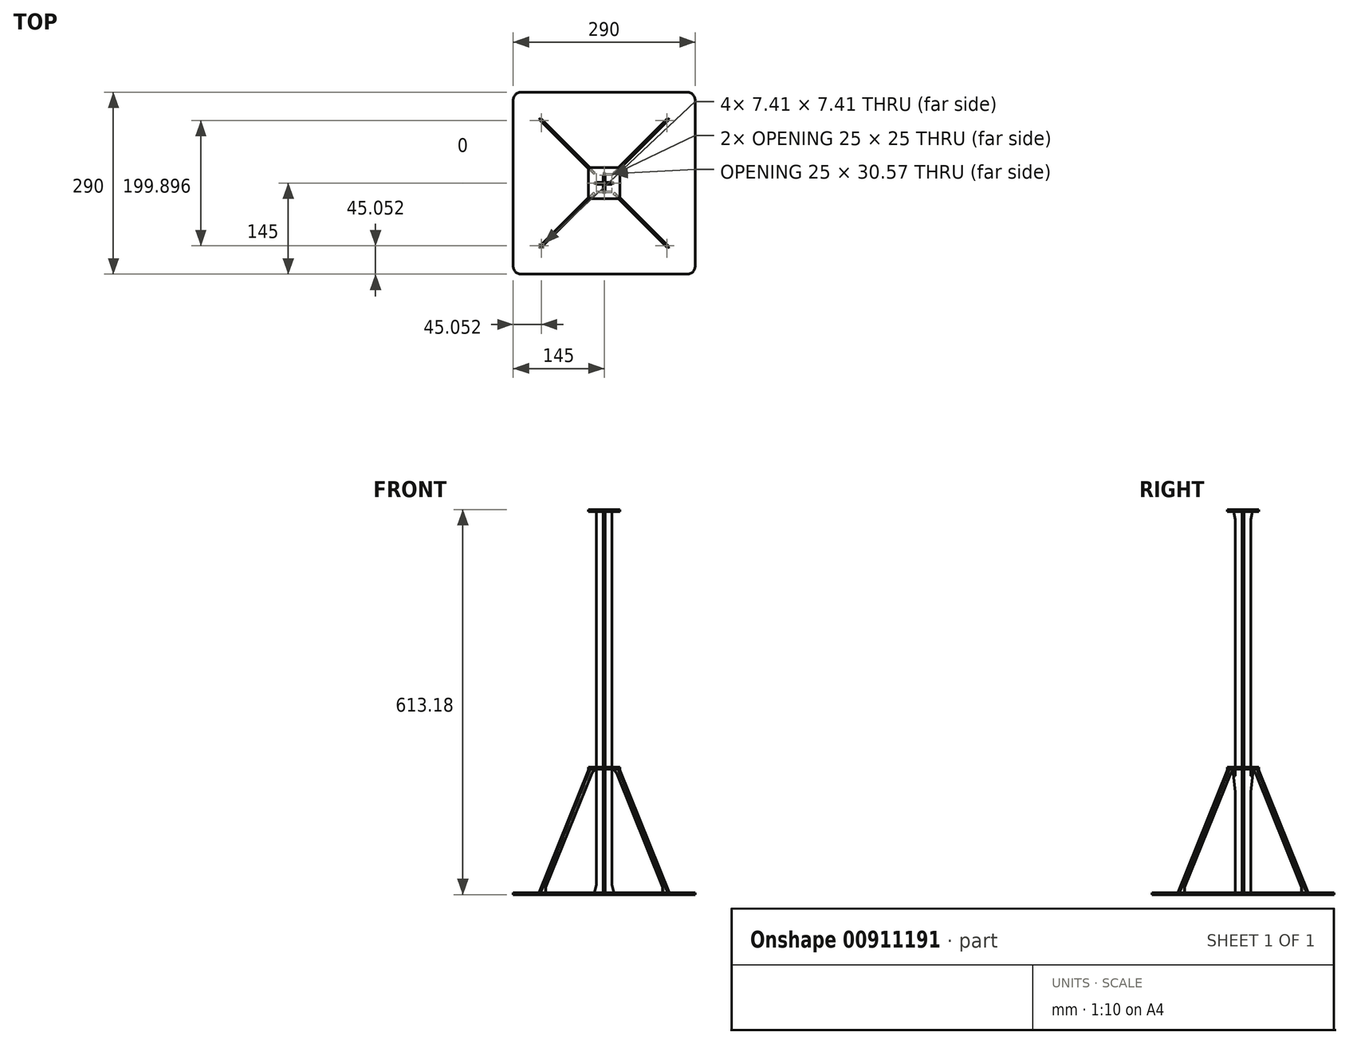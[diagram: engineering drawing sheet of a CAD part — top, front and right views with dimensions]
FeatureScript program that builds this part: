
annotation { "Feature Type Name" : "Feature", "Feature Type Description" : "" }
export const myFeature = defineFeature(function(context is Context, id is Id, definition is map)
    precondition{}
    {
        {
            assignVariable(context, id + "F0", {"variableType" : VariableType.LENGTH, "name" : "Thickness", "lengthValue" : 3.17 * mm});
        }
        {
            var Q0;
            Q0=qCreatedBy(makeId("Top.planeOp"),FACE);
            var sketch = newSketch(context, id + "F1", { "sketchPlane" : qUnion([Q0])});
            skLineSegment(sketch, "E0.bottom", {"start": v(-145, 145) * mm, "end": v(145, 145) * mm});
            skLineSegment(sketch, "E0.top", {"start": v(-145, -145) * mm, "end": v(145, -145) * mm});
            skLineSegment(sketch, "E0.left", {"start": v(-145, 145) * mm, "end": v(-145, -145) * mm});
            skLineSegment(sketch, "E0.right", {"start": v(145, 145) * mm, "end": v(145, -145) * mm});
            skPoint(sketch, "E0.middle", {"position": v(0, 0) * mm});
            skCircle(sketch, "E1", {"center": v(0, 0) * mm, "radius": 145 * mm});
            skLineSegment(sketch, "E2", {"start": v(0, 0) * mm, "end": v(145, 145) * mm, "construction": true});
            skLineSegment(sketch, "E3", {"start": v(0, 0) * mm, "end": v(-145, 145) * mm, "construction": true});
            skLineSegment(sketch, "E4", {"start": v(0, 0) * mm, "end": v(145, -145) * mm, "construction": true});
            skLineSegment(sketch, "E5", {"start": v(0, 0) * mm, "end": v(-145, -145) * mm, "construction": true});
            skSolve(sketch);
        }
        {
            var Q0;
            Q0 = qSketchRegion(id + "F1", true);
            extrude(context, id + "F2", {"entities" : qUnion([Q0]), "depth" : getVariable(context, 'Thickness'), "offsetDistance" : 25.4 * mm});
        }
        {
            var Q0;
            Q0=qCreatedBy(makeId("Right.planeOp"),FACE);
            var sketch = newSketch(context, id + "F3", { "sketchPlane" : qUnion([Q0])});
            skLineSegment(sketch, "E6.bottom", {"start": v(-12.5, 0) * mm, "end": v(12.5, 0) * mm});
            skLineSegment(sketch, "E6.top", {"start": v(-12.5, 613.18) * mm, "end": v(12.5, 613.18) * mm});
            skLineSegment(sketch, "E6.left", {"start": v(-12.5, 0) * mm, "end": v(-12.5, 163.77) * mm});
            skLineSegment(sketch, "E6.right", {"start": v(12.5, 189.19) * mm, "end": v(12.5, 597.3) * mm});
            skPoint(sketch, "E6.middle", {"position": v(0, 306.59) * mm});
            skLineSegment(sketch, "E7", {"start": v(12.5, 203.18) * mm, "end": v(-12.5, 203.18) * mm, "construction": true});
            skLineSegment(sketch, "E8.bottom", {"start": v(25, 203.18) * mm, "end": v(-25, 203.18) * mm, "construction": true});
            skLineSegment(sketch, "E8.top", {"start": v(25, 200) * mm, "end": v(-25, 200) * mm, "construction": true});
            skLineSegment(sketch, "E8.left", {"start": v(25, 203.18) * mm, "end": v(25, 200) * mm, "construction": true});
            skLineSegment(sketch, "E8.right", {"start": v(-25, 203.18) * mm, "end": v(-25, 200) * mm, "construction": true});
            skPoint(sketch, "E8.middle", {"position": v(0, 201.59) * mm});
            skPoint(sketch, "E8.middle.positionSnap0", {"position": v(0, 203.18) * mm});
            skPoint(sketch, "E8.cornerSnap0", {"position": v(0, 203.18) * mm});
            skPoint(sketch, "E8.centerSnap0", {"position": v(0, 203.18) * mm});
            skLineSegment(sketch, "E9.bottom", {"start": v(-15, 613.18) * mm, "end": v(15, 613.18) * mm, "construction": true});
            skLineSegment(sketch, "E9.top", {"start": v(-15, 610) * mm, "end": v(15, 610) * mm, "construction": true});
            skLineSegment(sketch, "E9.left", {"start": v(-15, 613.18) * mm, "end": v(-15, 610) * mm, "construction": true});
            skLineSegment(sketch, "E9.right", {"start": v(15, 613.18) * mm, "end": v(15, 610) * mm, "construction": true});
            skPoint(sketch, "E9.middle", {"position": v(0, 611.59) * mm});
            skLineSegment(sketch, "E10", {"start": v(15, 610) * mm, "end": v(12.5, 597.3) * mm});
            skLineSegment(sketch, "E11", {"start": v(16.48, 200) * mm, "end": v(12.5, 163.8) * mm});
            skLineSegment(sketch, "E12", {"start": v(14.09, 200) * mm, "end": v(12.9, 189.16) * mm});
            skArc(sketch, "E13.filletArc", {"start": v(12.5, 189.19) * mm, "mid": v(12.69, 188.99) * mm, "end": v(12.9, 189.16) * mm});
            skLineSegment(sketch, "E14", {"start": v(12.5, 163.77) * mm, "end": v(12.5, 0) * mm});
            skPoint(sketch, "E15.visualSharp", {"position": v(12.5, 163.79) * mm});
            skArc(sketch, "E15.filletArc", {"start": v(12.5, 163.8) * mm, "mid": v(12.5, 163.79) * mm, "end": v(12.5, 163.77) * mm});
            skLineSegment(sketch, "E16", {"start": v(16.48, 200) * mm, "end": v(14.09, 200) * mm});
            skLineSegment(sketch, "E17.trimOffspring", {"start": v(12.5, 610) * mm, "end": v(12.5, 613.18) * mm});
            skLineSegment(sketch, "E18", {"start": v(15, 610) * mm, "end": v(12.5, 610) * mm});
            skLineSegment(sketch, "E19.MirrorCS", {"start": v(-14.09, 200) * mm, "end": v(-12.9, 189.16) * mm});
            skLineSegment(sketch, "E20.MirrorCS", {"start": v(-16.48, 200) * mm, "end": v(-12.5, 163.8) * mm});
            skArc(sketch, "E21.MirrorCS", {"start": v(-12.5, 189.19) * mm, "mid": v(-12.69, 188.99) * mm, "end": v(-12.9, 189.16) * mm});
            skArc(sketch, "E22.MirrorCS", {"start": v(-12.5, 163.8) * mm, "mid": v(-12.5, 163.79) * mm, "end": v(-12.5, 163.77) * mm});
            skLineSegment(sketch, "E23.MirrorCS", {"start": v(-15, 610) * mm, "end": v(-12.5, 597.3) * mm});
            skLineSegment(sketch, "E24", {"start": v(-12.5, 610) * mm, "end": v(-15, 610) * mm});
            skLineSegment(sketch, "E25", {"start": v(-14.09, 200) * mm, "end": v(-16.48, 200) * mm});
            skLineSegment(sketch, "E26.trimOffspring", {"start": v(-12.5, 189.19) * mm, "end": v(-12.5, 597.3) * mm});
            skLineSegment(sketch, "E27.bottom", {"start": v(-1.59, 613.18) * mm, "end": v(1.59, 613.18) * mm});
            skLineSegment(sketch, "E27.top", {"start": v(-1.59, 308.18) * mm, "end": v(1.59, 308.18) * mm});
            skLineSegment(sketch, "E27.left", {"start": v(-1.59, 613.18) * mm, "end": v(-1.59, 308.18) * mm});
            skLineSegment(sketch, "E27.right", {"start": v(1.59, 613.18) * mm, "end": v(1.59, 308.18) * mm});
            skPoint(sketch, "E27.middle", {"position": v(0, 460.68) * mm});
            skLineSegment(sketch, "E28.trimOffspring", {"start": v(-12.5, 610) * mm, "end": v(-12.5, 613.18) * mm});
            skLineSegment(sketch, "E29", {"start": v(0, 306.59) * mm, "end": v(0, 0) * mm, "construction": true});
            skSolve(sketch);
        }
        {
            var Q0;
            Q0=makeQuery(id+"F3.imprint","IMPRINT",FACE,{"disambiguationData":[TD([[makeQuery(id+"F3.imprint","IMPRINT",EDGE,{"derivedFrom":sQuery(id+"F3.wireOp",EDGE,"E6.bottom")}),1.0]])]});
            extrude(context, id + "F4", {"entities" : qUnion([Q0]), "endBound" : BoundingType.SYMMETRIC, "depth" : getVariable(context, 'Thickness'), "offsetDistance" : 25.4 * mm});
        }
        {
            var Q0;
            Q0=qCreatedBy(makeId("Front.planeOp"),FACE);
            var sketch = newSketch(context, id + "F5", { "sketchPlane" : qUnion([Q0])});
            skLineSegment(sketch, "E30.bottom", {"start": v(-12.5, 0) * mm, "end": v(12.5, 0) * mm});
            skLineSegment(sketch, "E30.top", {"start": v(-12.5, 613.18) * mm, "end": v(12.5, 613.18) * mm});
            skLineSegment(sketch, "E30.left", {"start": v(-12.5, 0) * mm, "end": v(-12.5, 3.18) * mm});
            skLineSegment(sketch, "E30.right", {"start": v(12.5, 0) * mm, "end": v(12.5, 3.18) * mm});
            skPoint(sketch, "E30.middle", {"position": v(0, 306.59) * mm});
            skLineSegment(sketch, "E31", {"start": v(12.5, 15.87) * mm, "end": v(15.68, 3.18) * mm});
            skLineSegment(sketch, "E32", {"start": v(15.68, 3.18) * mm, "end": v(12.5, 3.18) * mm});
            skLineSegment(sketch, "E33.trimOffspring", {"start": v(12.5, 15.88) * mm, "end": v(12.5, 613.18) * mm});
            skLineSegment(sketch, "E34.MirrorCS", {"start": v(-12.5, 15.87) * mm, "end": v(-15.68, 3.18) * mm});
            skLineSegment(sketch, "E35", {"start": v(-15.68, 3.18) * mm, "end": v(-12.5, 3.18) * mm});
            skLineSegment(sketch, "E36.trimOffspring", {"start": v(-12.5, 15.88) * mm, "end": v(-12.5, 613.18) * mm});
            skSolve(sketch);
        }
        {
            var Q0;
            Q0 = qSketchRegion(id + "F5", true);
            extrude(context, id + "F6", {"entities" : qUnion([Q0]), "endBound" : BoundingType.SYMMETRIC, "depth" : getVariable(context, 'Thickness'), "offsetDistance" : 25.4 * mm});
        }
        {
            var Q0;
            Q0=makeQuery(id+"F4.opExtrude","SWEPT_BODY",BODY,{"disambiguationData":[OSD([sQuery(id+"F3.wireOp",EDGE,"E6.bottom"),sQuery(id+"F3.wireOp",EDGE,"E6.top"),sQuery(id+"F3.wireOp",EDGE,"E6.left"),sQuery(id+"F3.wireOp",EDGE,"E6.right"),sQuery(id+"F3.wireOp",EDGE,"E10"),sQuery(id+"F3.wireOp",EDGE,"E11"),sQuery(id+"F3.wireOp",EDGE,"E12"),sQuery(id+"F3.wireOp",EDGE,"E13.filletArc"),sQuery(id+"F3.wireOp",EDGE,"E14"),sQuery(id+"F3.wireOp",EDGE,"E15.filletArc"),sQuery(id+"F3.wireOp",EDGE,"E16"),sQuery(id+"F3.wireOp",EDGE,"E17.trimOffspring"),sQuery(id+"F3.wireOp",EDGE,"E18"),sQuery(id+"F3.wireOp",EDGE,"E19.MirrorCS"),sQuery(id+"F3.wireOp",EDGE,"E20.MirrorCS"),sQuery(id+"F3.wireOp",EDGE,"E21.MirrorCS"),sQuery(id+"F3.wireOp",EDGE,"E22.MirrorCS"),sQuery(id+"F3.wireOp",EDGE,"E23.MirrorCS"),sQuery(id+"F3.wireOp",EDGE,"E24"),sQuery(id+"F3.wireOp",EDGE,"E25"),sQuery(id+"F3.wireOp",EDGE,"E26.trimOffspring"),sQuery(id+"F3.wireOp",EDGE,"E27.top"),sQuery(id+"F3.wireOp",EDGE,"E27.left"),sQuery(id+"F3.wireOp",EDGE,"E27.right"),sQuery(id+"F3.wireOp",EDGE,"E28.trimOffspring")])]});
            var Q1;
            Q1=makeQuery(id+"F6.opExtrude","SWEPT_BODY",BODY,{"disambiguationData":[OSD([sQuery(id+"F5.wireOp",EDGE,"E30.bottom"),sQuery(id+"F5.wireOp",EDGE,"E30.top"),sQuery(id+"F5.wireOp",EDGE,"E30.left"),sQuery(id+"F5.wireOp",EDGE,"E30.right"),sQuery(id+"F5.wireOp",EDGE,"E31"),sQuery(id+"F5.wireOp",EDGE,"E32"),sQuery(id+"F5.wireOp",EDGE,"E33.trimOffspring"),sQuery(id+"F5.wireOp",EDGE,"E34.MirrorCS"),sQuery(id+"F5.wireOp",EDGE,"E35"),sQuery(id+"F5.wireOp",EDGE,"E36.trimOffspring")])]});
            booleanBodies(context, id + "F7", {"operationType" : BooleanOperationType.SUBTRACTION, "tools" : qUnion([Q0]), "targets" : qUnion([Q1]), "keepTools" : true});
        }
        {
            var Q0;
            Q0=makeQuery(id+"F4.opExtrude","SWEPT_FACE",FACE,{"disambiguationData":[OSD([sQuery(id+"F3.wireOp",EDGE,"E24")])]});
            var sketch = newSketch(context, id + "F8", { "sketchPlane" : qUnion([Q0])});
            skLineSegment(sketch, "E37.bottom", {"start": v(-25, 25) * mm, "end": v(25, 25) * mm});
            skLineSegment(sketch, "E37.top", {"start": v(-25, -25) * mm, "end": v(25, -25) * mm});
            skLineSegment(sketch, "E37.left", {"start": v(-25, 25) * mm, "end": v(-25, -25) * mm});
            skLineSegment(sketch, "E37.right", {"start": v(25, 25) * mm, "end": v(25, -25) * mm});
            skPoint(sketch, "E37.middle", {"position": v(0, 0) * mm});
            skSolve(sketch);
        }
        {
            var Q0;
            Q0 = qSketchRegion(id + "F8", true);
            extrude(context, id + "F9", {"entities" : qUnion([Q0]), "depth" : getVariable(context, 'Thickness'), "offsetDistance" : 25.4 * mm});
        }
        {
            var Q0;
            Q0=makeQuery(id+"F4.opExtrude","SWEPT_FACE",FACE,{"disambiguationData":[OSD([sQuery(id+"F3.wireOp",EDGE,"E16")])]});
            var sketch = newSketch(context, id + "F10", { "sketchPlane" : qUnion([Q0])});
            skLineSegment(sketch, "E38.bottom", {"start": v(25, 25) * mm, "end": v(-25, 25) * mm});
            skLineSegment(sketch, "E38.top", {"start": v(25, -25) * mm, "end": v(-25, -25) * mm});
            skLineSegment(sketch, "E38.left", {"start": v(25, 25) * mm, "end": v(25, -25) * mm});
            skLineSegment(sketch, "E38.right", {"start": v(-25, 25) * mm, "end": v(-25, -25) * mm});
            skPoint(sketch, "E38.middle", {"position": v(0, 0) * mm});
            skPoint(sketch, "E39.0", {"position": v(-1.59, 15.29) * mm});
            skPoint(sketch, "E40.0", {"position": v(0, 16.48) * mm});
            skPoint(sketch, "E41", {"position": v(0, 15.29) * mm});
            skLineSegment(sketch, "E42.bottom", {"start": v(-1.59, 15.29) * mm, "end": v(1.59, 15.29) * mm});
            skLineSegment(sketch, "E42.top", {"start": v(-1.59, -15.29) * mm, "end": v(1.59, -15.29) * mm});
            skLineSegment(sketch, "E42.left", {"start": v(-1.59, 15.29) * mm, "end": v(-1.59, -15.29) * mm});
            skLineSegment(sketch, "E42.right", {"start": v(1.59, 15.29) * mm, "end": v(1.59, -15.29) * mm});
            skSolve(sketch);
        }
        {
            var Q0;
            Q0 = qSketchRegion(id + "F10", true);
            extrude(context, id + "F11", {"entities" : qUnion([Q0]), "depth" : getVariable(context, 'Thickness'), "offsetDistance" : 25.4 * mm});
        }
        {
            var Q0;
            Q0=makeQuery(id+"F9.opExtrude","SWEPT_EDGE",EDGE,{"disambiguationData":[OSD([sQuery(id+"F8.wireOp",EDGE,"E37.top"),sQuery(id+"F8.wireOp",EDGE,"E37.left")])]});
            var Q1;
            Q1=makeQuery(id+"F9.opExtrude","SWEPT_EDGE",EDGE,{"disambiguationData":[OSD([sQuery(id+"F8.wireOp",EDGE,"E37.top"),sQuery(id+"F8.wireOp",EDGE,"E37.right")])]});
            var Q2;
            Q2=makeQuery(id+"F9.opExtrude","SWEPT_EDGE",EDGE,{"disambiguationData":[OSD([sQuery(id+"F8.wireOp",EDGE,"E37.bottom"),sQuery(id+"F8.wireOp",EDGE,"E37.right")])]});
            var Q3;
            Q3=makeQuery(id+"F9.opExtrude","SWEPT_EDGE",EDGE,{"disambiguationData":[OSD([sQuery(id+"F8.wireOp",EDGE,"E37.bottom"),sQuery(id+"F8.wireOp",EDGE,"E37.left")])]});
            var Q4;
            Q4=makeQuery(id+"F11.opExtrude","SWEPT_EDGE",EDGE,{"disambiguationData":[OSD([sQuery(id+"F10.wireOp",EDGE,"E38.bottom"),sQuery(id+"F10.wireOp",EDGE,"E38.right")])]});
            var Q5;
            Q5=makeQuery(id+"F11.opExtrude","SWEPT_EDGE",EDGE,{"disambiguationData":[OSD([sQuery(id+"F10.wireOp",EDGE,"E38.bottom"),sQuery(id+"F10.wireOp",EDGE,"E38.left")])]});
            var Q6;
            Q6=makeQuery(id+"F11.opExtrude","SWEPT_EDGE",EDGE,{"disambiguationData":[OSD([sQuery(id+"F10.wireOp",EDGE,"E38.top"),sQuery(id+"F10.wireOp",EDGE,"E38.right")])]});
            var Q7;
            Q7=makeQuery(id+"F11.opExtrude","SWEPT_EDGE",EDGE,{"disambiguationData":[OSD([sQuery(id+"F10.wireOp",EDGE,"E38.top"),sQuery(id+"F10.wireOp",EDGE,"E38.left")])]});
            chamfer(context, id + "F12", {"entities" : qUnion([Q0, Q1, Q2, Q3, Q4, Q5, Q6, Q7]), "width" : 3.17 * mm, "tangentPropagation" : true});
        }
        {
            var Q0;
            Q0=sQuery(id+"F1.wireOp",EDGE,"E5");
            cPlane(context, id + "F13", {"entities" : qUnion([Q0]), "cplaneType" : CPlaneType.LINE_ANGLE, "offset" : 25.4 * mm, "angle" : 90 * degree, "width" : 152.4 * mm, "height" : 152.4 * mm});
        }
        {
            var Q0;
            Q0=qCreatedBy(id+"F13.planeOp",FACE);
            var sketch = newSketch(context, id + "F14", { "sketchPlane" : qUnion([Q0])});
            skPoint(sketch, "E43.0", {"position": v(-31.3, 203.18) * mm});
            skLineSegment(sketch, "E44", {"start": v(-33.11, 200) * mm, "end": v(-145, 3.17) * mm});
            skLineSegment(sketch, "E45", {"start": v(-132.93, 11.55) * mm, "end": v(-29.42, 193.65) * mm});
            skLineSegment(sketch, "E46", {"start": v(-132.93, 11.55) * mm, "end": v(-132.93, 3.18) * mm});
            skLineSegment(sketch, "E47", {"start": v(-145, 3.18) * mm, "end": v(-145, 0) * mm});
            skLineSegment(sketch, "E48", {"start": v(-145, 0) * mm, "end": v(-137.7, 0) * mm});
            skLineSegment(sketch, "E49", {"start": v(-137.7, 0) * mm, "end": v(-137.7, 3.18) * mm});
            skLineSegment(sketch, "E50", {"start": v(-29.42, 193.65) * mm, "end": v(-22.15, 200) * mm});
            skLineSegment(sketch, "E51.0", {"start": v(-2.25, 200) * mm, "end": v(-33.11, 200) * mm});
            skPoint(sketch, "E52.0", {"position": v(-33.11, 200) * mm});
            skPoint(sketch, "E53.orphan", {"position": v(-24, 203.18) * mm});
            skLineSegment(sketch, "E54", {"start": v(-33.11, 200) * mm, "end": v(-33.11, 203.18) * mm});
            skLineSegment(sketch, "E55", {"start": v(-33.11, 203.18) * mm, "end": v(-25.8, 203.18) * mm});
            skLineSegment(sketch, "E56", {"start": v(-25.8, 203.18) * mm, "end": v(-25.8, 200) * mm});
            skLineSegment(sketch, "E57", {"start": v(-137.7, 3.18) * mm, "end": v(-132.93, 3.18) * mm});
            skLineSegment(sketch, "E58.0", {"start": v(-145, 0) * mm, "end": v(145, 0) * mm});
            skLineSegment(sketch, "E58.1", {"start": v(0, 0) * mm, "end": v(-205.06, 0) * mm});
            skSolve(sketch);
        }
        {
            var Q0;
            Q0 = qSketchRegion(id + "F14", true);
            extrude(context, id + "F15", {"entities" : qUnion([Q0]), "endBound" : BoundingType.SYMMETRIC, "depth" : getVariable(context, 'Thickness'), "offsetDistance" : 25.4 * mm});
        }
        {
            var Q0;
            Q0=makeQuery(id+"F15.opExtrude","SWEPT_BODY",BODY,{"disambiguationData":[OSD([sQuery(id+"F14.wireOp",EDGE,"E44"),sQuery(id+"F14.wireOp",EDGE,"E45"),sQuery(id+"F14.wireOp",EDGE,"E46"),sQuery(id+"F14.wireOp",EDGE,"E47"),sQuery(id+"F14.wireOp",EDGE,"E48"),sQuery(id+"F14.wireOp",EDGE,"E49"),sQuery(id+"F14.wireOp",EDGE,"E50"),sQuery(id+"F14.wireOp",EDGE,"E51.0"),sQuery(id+"F14.wireOp",EDGE,"E54"),sQuery(id+"F14.wireOp",EDGE,"E55"),sQuery(id+"F14.wireOp",EDGE,"E56"),sQuery(id+"F14.wireOp",EDGE,"E57")])]});
            var Q1;
            Q1=sQuery(id+"F3.wireOp",EDGE,"E29");
            circularPattern(context, id + "F16", {"entities" : qUnion([Q0]), "axis" : qUnion([Q1]), "angle" : 360 * degree, "instanceCount" : 4, "equalSpace" : true});
        }
        {
            var Q0;
            Q0=makeQuery(id+"F6.opExtrude","SWEPT_BODY",BODY,{"disambiguationData":[OSD([sQuery(id+"F5.wireOp",EDGE,"E30.bottom"),sQuery(id+"F5.wireOp",EDGE,"E30.top"),sQuery(id+"F5.wireOp",EDGE,"E30.left"),sQuery(id+"F5.wireOp",EDGE,"E30.right"),sQuery(id+"F5.wireOp",EDGE,"E31"),sQuery(id+"F5.wireOp",EDGE,"E32"),sQuery(id+"F5.wireOp",EDGE,"E33.trimOffspring"),sQuery(id+"F5.wireOp",EDGE,"E34.MirrorCS"),sQuery(id+"F5.wireOp",EDGE,"E35"),sQuery(id+"F5.wireOp",EDGE,"E36.trimOffspring")])]});
            var Q1;
            Q1=makeQuery(id+"F4.opExtrude","SWEPT_BODY",BODY,{"disambiguationData":[OSD([sQuery(id+"F3.wireOp",EDGE,"E6.bottom"),sQuery(id+"F3.wireOp",EDGE,"E6.top"),sQuery(id+"F3.wireOp",EDGE,"E6.left"),sQuery(id+"F3.wireOp",EDGE,"E6.right"),sQuery(id+"F3.wireOp",EDGE,"E10"),sQuery(id+"F3.wireOp",EDGE,"E11"),sQuery(id+"F3.wireOp",EDGE,"E12"),sQuery(id+"F3.wireOp",EDGE,"E13.filletArc"),sQuery(id+"F3.wireOp",EDGE,"E14"),sQuery(id+"F3.wireOp",EDGE,"E15.filletArc"),sQuery(id+"F3.wireOp",EDGE,"E16"),sQuery(id+"F3.wireOp",EDGE,"E17.trimOffspring"),sQuery(id+"F3.wireOp",EDGE,"E18"),sQuery(id+"F3.wireOp",EDGE,"E19.MirrorCS"),sQuery(id+"F3.wireOp",EDGE,"E20.MirrorCS"),sQuery(id+"F3.wireOp",EDGE,"E21.MirrorCS"),sQuery(id+"F3.wireOp",EDGE,"E22.MirrorCS"),sQuery(id+"F3.wireOp",EDGE,"E23.MirrorCS"),sQuery(id+"F3.wireOp",EDGE,"E24"),sQuery(id+"F3.wireOp",EDGE,"E25"),sQuery(id+"F3.wireOp",EDGE,"E26.trimOffspring"),sQuery(id+"F3.wireOp",EDGE,"E27.top"),sQuery(id+"F3.wireOp",EDGE,"E27.left"),sQuery(id+"F3.wireOp",EDGE,"E27.right"),sQuery(id+"F3.wireOp",EDGE,"E28.trimOffspring")])]});
            var Q2;
            Q2=makeQuery(id+"F15.opExtrude","SWEPT_BODY",BODY,{"disambiguationData":[OSD([sQuery(id+"F14.wireOp",EDGE,"1f06c835-850c-4332-a980-dfa636498e00.0"),sQuery(id+"F14.wireOp",EDGE,"E44"),sQuery(id+"F14.wireOp",EDGE,"E45"),sQuery(id+"F14.wireOp",EDGE,"E46"),sQuery(id+"F14.wireOp",EDGE,"E47"),sQuery(id+"F14.wireOp",EDGE,"E48"),sQuery(id+"F14.wireOp",EDGE,"E49"),sQuery(id+"F14.wireOp",EDGE,"E50"),sQuery(id+"F14.wireOp",EDGE,"E51.0"),sQuery(id+"F14.wireOp",EDGE,"E54"),sQuery(id+"F14.wireOp",EDGE,"E55"),sQuery(id+"F14.wireOp",EDGE,"E56")])]});
            var Q3;
            Q3=makeQuery(id+"F16.opPattern","COPY",BODY,{"derivedFrom":makeQuery(id+"F15.opExtrude","SWEPT_BODY",BODY,{"disambiguationData":[OSD([sQuery(id+"F14.wireOp",EDGE,"E44"),sQuery(id+"F14.wireOp",EDGE,"E45"),sQuery(id+"F14.wireOp",EDGE,"E46"),sQuery(id+"F14.wireOp",EDGE,"E47"),sQuery(id+"F14.wireOp",EDGE,"E48"),sQuery(id+"F14.wireOp",EDGE,"E49"),sQuery(id+"F14.wireOp",EDGE,"E50"),sQuery(id+"F14.wireOp",EDGE,"E51.0"),sQuery(id+"F14.wireOp",EDGE,"E54"),sQuery(id+"F14.wireOp",EDGE,"E55"),sQuery(id+"F14.wireOp",EDGE,"E56"),sQuery(id+"F14.wireOp",EDGE,"E57")])]}),"instanceName":"3"});
            var Q4;
            Q4=makeQuery(id+"F16.opPattern","COPY",BODY,{"derivedFrom":makeQuery(id+"F15.opExtrude","SWEPT_BODY",BODY,{"disambiguationData":[OSD([sQuery(id+"F14.wireOp",EDGE,"E44"),sQuery(id+"F14.wireOp",EDGE,"E45"),sQuery(id+"F14.wireOp",EDGE,"E46"),sQuery(id+"F14.wireOp",EDGE,"E47"),sQuery(id+"F14.wireOp",EDGE,"E48"),sQuery(id+"F14.wireOp",EDGE,"E49"),sQuery(id+"F14.wireOp",EDGE,"E50"),sQuery(id+"F14.wireOp",EDGE,"E51.0"),sQuery(id+"F14.wireOp",EDGE,"E54"),sQuery(id+"F14.wireOp",EDGE,"E55"),sQuery(id+"F14.wireOp",EDGE,"E56"),sQuery(id+"F14.wireOp",EDGE,"E57")])]}),"instanceName":"2"});
            var Q5;
            Q5=makeQuery(id+"F16.opPattern","COPY",BODY,{"derivedFrom":makeQuery(id+"F15.opExtrude","SWEPT_BODY",BODY,{"disambiguationData":[OSD([sQuery(id+"F14.wireOp",EDGE,"E44"),sQuery(id+"F14.wireOp",EDGE,"E45"),sQuery(id+"F14.wireOp",EDGE,"E46"),sQuery(id+"F14.wireOp",EDGE,"E47"),sQuery(id+"F14.wireOp",EDGE,"E48"),sQuery(id+"F14.wireOp",EDGE,"E49"),sQuery(id+"F14.wireOp",EDGE,"E50"),sQuery(id+"F14.wireOp",EDGE,"E51.0"),sQuery(id+"F14.wireOp",EDGE,"E54"),sQuery(id+"F14.wireOp",EDGE,"E55"),sQuery(id+"F14.wireOp",EDGE,"E56"),sQuery(id+"F14.wireOp",EDGE,"E57")])]}),"instanceName":"1"});
            var Q6;
            Q6=makeQuery(id+"F2.opExtrude","SWEPT_BODY",BODY,{"disambiguationData":[OSD([sQuery(id+"F1.wireOp",EDGE,"E0.bottom"),sQuery(id+"F1.wireOp",EDGE,"E0.top"),sQuery(id+"F1.wireOp",EDGE,"E0.left"),sQuery(id+"F1.wireOp",EDGE,"E0.right")])]});
            var Q7;
            Q7=makeQuery(id+"F9.opExtrude","SWEPT_BODY",BODY,{"disambiguationData":[OSD([sQuery(id+"F8.wireOp",EDGE,"E37.bottom"),sQuery(id+"F8.wireOp",EDGE,"E37.top"),sQuery(id+"F8.wireOp",EDGE,"E37.left"),sQuery(id+"F8.wireOp",EDGE,"E37.right")])]});
            var Q8;
            Q8=makeQuery(id+"F11.opExtrude","SWEPT_BODY",BODY,{"disambiguationData":[OSD([sQuery(id+"F10.wireOp",EDGE,"E38.bottom"),sQuery(id+"F10.wireOp",EDGE,"E38.top"),sQuery(id+"F10.wireOp",EDGE,"E38.left"),sQuery(id+"F10.wireOp",EDGE,"E38.right")])]});
            booleanBodies(context, id + "F17", {"operationType" : BooleanOperationType.SUBTRACTION, "tools" : qUnion([Q0, Q1, Q2, Q3, Q4, Q5]), "targets" : qUnion([Q6, Q7, Q8]), "keepTools" : true});
        }
        {
            var Q0;
            Q0=makeQuery(id+"F2.opExtrude","SWEPT_EDGE",EDGE,{"disambiguationData":[OSD([sQuery(id+"F1.wireOp",EDGE,"E0.bottom"),sQuery(id+"F1.wireOp",EDGE,"E0.left")])]});
            var Q1;
            Q1=makeQuery(id+"F2.opExtrude","SWEPT_EDGE",EDGE,{"disambiguationData":[OSD([sQuery(id+"F1.wireOp",EDGE,"E0.top"),sQuery(id+"F1.wireOp",EDGE,"E0.left")])]});
            var Q2;
            Q2=makeQuery(id+"F2.opExtrude","SWEPT_EDGE",EDGE,{"disambiguationData":[OSD([sQuery(id+"F1.wireOp",EDGE,"E0.top"),sQuery(id+"F1.wireOp",EDGE,"E0.right")])]});
            var Q3;
            Q3=makeQuery(id+"F2.opExtrude","SWEPT_EDGE",EDGE,{"disambiguationData":[OSD([sQuery(id+"F1.wireOp",EDGE,"E0.bottom"),sQuery(id+"F1.wireOp",EDGE,"E0.right")])]});
            fillet(context, id + "F18", {"entities" : qUnion([Q0, Q1, Q2, Q3]), "tangentPropagation" : true, "radius" : 12.7 * mm, "defaultsChanged" : true, "vertexSettings" : [], "allowEdgeOverflow" : false});
        }
    });
